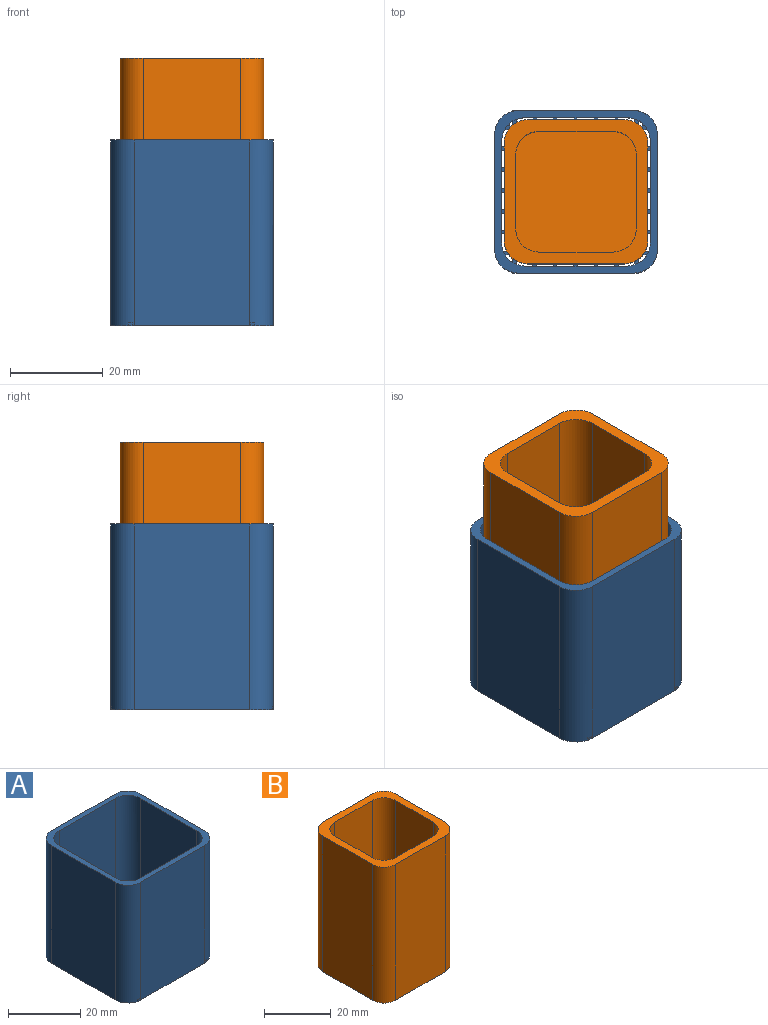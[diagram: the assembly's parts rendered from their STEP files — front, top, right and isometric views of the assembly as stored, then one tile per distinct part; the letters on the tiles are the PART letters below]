
ASSEMBLY  parts=2 mates=1
PART A: 259 faces, bbox 35x35x40 mm
  f0: plane 3.7x0.6mm, normal (-1,0,0), area 2.2mm2, adj f115,f120,f242,f257
  f1: cylinder r=5mm len=40mm, axis (0,0,-1), area 313mm2, adj f17,f112,f114,f115,f120,f137,f138,f257
  f2: plane 3.7x0.6mm, normal (-1,0,0), area 2.2mm2, adj f115,f120,f240,f255
  f3: plane 3.7x0.6mm, normal (1,0,0), area 2.2mm2, adj f115,f120,f240,f255
  f4: plane 3.7x0.6mm, normal (-1,0,0), area 2.2mm2, adj f115,f120,f238,f253
  f5: plane 3.7x0.6mm, normal (1,0,0), area 2.2mm2, adj f115,f120,f238,f253
  f6: plane 3.7x0.6mm, normal (-1,0,0), area 2.2mm2, adj f115,f120,f236,f251
  f7: plane 3.7x0.6mm, normal (1,0,0), area 2.2mm2, adj f115,f120,f236,f251
  f8: plane 3.7x0.6mm, normal (-1,0,0), area 2.2mm2, adj f115,f120,f234,f249
  f9: plane 3.7x0.6mm, normal (1,0,0), area 2.2mm2, adj f115,f120,f234,f249
  f10: plane 3.7x0.6mm, normal (-1,0,0), area 2.2mm2, adj f115,f120,f232,f247
  f11: plane 3.7x0.6mm, normal (1,0,0), area 2.2mm2, adj f115,f120,f232,f247
  f12: plane 3.7x0.6mm, normal (-1,0,0), area 2.2mm2, adj f115,f120,f230,f245
  f13: plane 3.7x0.6mm, normal (1,0,0), area 2.2mm2, adj f115,f120,f230,f245
  f14: plane 3.7x0.6mm, normal (1,0,0), area 2.2mm2, adj f115,f120,f228,f243
  f15: cylinder r=5mm len=40mm, axis (0,0,-1), area 313mm2, adj f31,f112,f114,f115,f120,f121,f122,f243
  f16: plane 3.7x0.6mm, normal (-1,0,0), area 2.2mm2, adj f115,f120,f226,f241
  f17: plane 40x22mm, normal (1,0,0), area 877.6mm2, adj f1,f89,f114,f115,f120,f163,f164,f187
  f18: plane 3.7x0.6mm, normal (-1,0,0), area 2.2mm2, adj f115,f120,f224,f239
  f19: plane 3.7x0.6mm, normal (1,0,0), area 2.2mm2, adj f115,f120,f224,f239
  f20: plane 3.7x0.6mm, normal (-1,0,0), area 2.2mm2, adj f115,f120,f222,f237
  f21: plane 3.7x0.6mm, normal (1,0,0), area 2.2mm2, adj f115,f120,f222,f237
  f22: plane 3.7x0.6mm, normal (-1,0,0), area 2.2mm2, adj f115,f120,f219,f235
  f23: plane 3.7x0.6mm, normal (1,0,0), area 2.2mm2, adj f115,f120,f219,f235
  f24: plane 3.7x0.6mm, normal (-1,0,0), area 2.2mm2, adj f115,f120,f217,f233
  f25: plane 3.7x0.6mm, normal (1,0,0), area 2.2mm2, adj f115,f120,f217,f233
  f26: plane 3.7x0.6mm, normal (-1,0,0), area 2.2mm2, adj f115,f120,f216,f231
  f27: plane 3.7x0.6mm, normal (1,0,0), area 2.2mm2, adj f115,f120,f216,f231
  f28: plane 3.7x0.6mm, normal (-1,0,0), area 2.2mm2, adj f115,f120,f214,f229
  f29: plane 3.7x0.6mm, normal (1,0,0), area 2.2mm2, adj f115,f120,f214,f229
  f30: plane 3.7x0.6mm, normal (1,0,0), area 2.2mm2, adj f115,f120,f212,f227
  f31: plane 40x22mm, normal (-1,0,0), area 877.6mm2, adj f15,f88,f114,f115,f120,f177,f178,f179
  f32: plane 3.7x0.6mm, normal (-1,0,0), area 2.2mm2, adj f115,f120,f210,f225
  f33: plane 3.7x0.6mm, normal (-1,0,0), area 2.2mm2, adj f115,f120,f207,f223
  f34: plane 3.7x0.6mm, normal (1,0,0), area 2.2mm2, adj f115,f120,f207,f223
  f35: plane 3.7x0.6mm, normal (-1,0,0), area 2.2mm2, adj f115,f120,f206,f221
  f36: plane 3.7x0.6mm, normal (1,0,0), area 2.2mm2, adj f115,f120,f206,f221
  f37: plane 3.7x0.6mm, normal (-1,0,0), area 2.2mm2, adj f115,f120,f203,f220
  f38: plane 3.7x0.6mm, normal (1,0,0), area 2.2mm2, adj f115,f120,f203,f220
  f39: plane 3.7x0.6mm, normal (-1,0,0), area 2.2mm2, adj f115,f120,f202,f218
  f40: plane 3.7x0.6mm, normal (1,0,0), area 2.2mm2, adj f115,f120,f202,f218
  f41: plane 3.7x0.6mm, normal (-1,0,0), area 2.2mm2, adj f115,f120,f200,f215
  f42: plane 3.7x0.6mm, normal (1,0,0), area 2.2mm2, adj f115,f120,f200,f215
  f43: plane 3.7x0.6mm, normal (-1,0,0), area 2.2mm2, adj f115,f120,f198,f213
  f44: plane 3.7x0.6mm, normal (1,0,0), area 2.2mm2, adj f115,f120,f198,f213
  f45: plane 3.7x0.6mm, normal (1,0,0), area 2.2mm2, adj f115,f120,f196,f211
  f46: plane 3.7x0.6mm, normal (-1,0,0), area 2.2mm2, adj f115,f120,f188,f209
  f47: plane 3.7x0.6mm, normal (-1,0,0), area 2.2mm2, adj f115,f120,f190,f208
  f48: plane 3.7x0.6mm, normal (1,0,0), area 2.2mm2, adj f115,f120,f190,f208
  f49: plane 3.7x0.6mm, normal (-1,0,0), area 2.2mm2, adj f115,f120,f192,f205
  f50: plane 3.7x0.6mm, normal (1,0,0), area 2.2mm2, adj f115,f120,f192,f205
  f51: plane 3.7x0.6mm, normal (-1,0,0), area 2.2mm2, adj f115,f120,f193,f204
  f52: plane 3.7x0.6mm, normal (1,0,0), area 2.2mm2, adj f115,f120,f193,f204
  f53: plane 3.7x0.6mm, normal (-1,0,0), area 2.2mm2, adj f115,f120,f186,f201
  f54: plane 3.7x0.6mm, normal (1,0,0), area 2.2mm2, adj f115,f120,f186,f201
  f55: plane 3.7x0.6mm, normal (-1,0,0), area 2.2mm2, adj f115,f120,f184,f199
  f56: plane 3.7x0.6mm, normal (1,0,0), area 2.2mm2, adj f115,f120,f184,f199
  f57: plane 3.7x0.6mm, normal (-1,0,0), area 2.2mm2, adj f115,f120,f182,f197
  f58: plane 3.7x0.6mm, normal (1,0,0), area 2.2mm2, adj f115,f120,f182,f197
  f59: plane 3.7x0.6mm, normal (1,0,0), area 2.2mm2, adj f115,f120,f180,f195
  f60: plane 3.7x0.6mm, normal (-1,0,0), area 2.2mm2, adj f115,f120,f169,f194
  f61: plane 3.7x0.6mm, normal (-1,0,0), area 2.2mm2, adj f115,f120,f167,f191
  f62: plane 3.7x0.6mm, normal (1,0,0), area 2.2mm2, adj f115,f120,f169,f194
  f63: plane 3.7x0.6mm, normal (-1,0,0), area 2.2mm2, adj f115,f120,f165,f189
  f64: plane 3.7x0.6mm, normal (1,0,0), area 2.2mm2, adj f115,f120,f167,f191
  f65: plane 3.7x0.6mm, normal (1,0,0), area 2.2mm2, adj f115,f120,f165,f189
  f66: plane 3.7x0.6mm, normal (-1,0,0), area 2.2mm2, adj f115,f120,f163,f187
  f67: plane 3.7x0.6mm, normal (-1,0,0), area 2.2mm2, adj f115,f120,f171,f185
  f68: plane 3.7x0.6mm, normal (1,0,0), area 2.2mm2, adj f115,f120,f171,f185
  f69: plane 3.7x0.6mm, normal (-1,0,0), area 2.2mm2, adj f115,f120,f173,f183
  f70: plane 3.7x0.6mm, normal (1,0,0), area 2.2mm2, adj f115,f120,f173,f183
  f71: plane 3.7x0.6mm, normal (-1,0,0), area 2.2mm2, adj f115,f120,f175,f181
  f72: plane 3.7x0.6mm, normal (1,0,0), area 2.2mm2, adj f115,f120,f175,f181
  f73: plane 3.7x0.6mm, normal (1,0,0), area 2.2mm2, adj f115,f120,f178,f179
  f74: plane 3.7x0.6mm, normal (1,0,0), area 2.2mm2, adj f115,f120,f162,f177
  f75: plane 3.7x0.6mm, normal (-1,0,0), area 2.2mm2, adj f115,f120,f159,f176
  f76: plane 3.7x0.6mm, normal (-1,0,0), area 2.2mm2, adj f115,f120,f157,f174
  f77: plane 3.7x0.6mm, normal (1,0,0), area 2.2mm2, adj f115,f120,f159,f176
  f78: plane 3.7x0.6mm, normal (-1,0,0), area 2.2mm2, adj f115,f120,f155,f172
  f79: plane 3.7x0.6mm, normal (1,0,0), area 2.2mm2, adj f115,f120,f157,f174
  f80: plane 3.7x0.6mm, normal (-1,0,0), area 2.2mm2, adj f115,f120,f153,f170
  f81: plane 3.7x0.6mm, normal (1,0,0), area 2.2mm2, adj f115,f120,f155,f172
  f82: plane 3.7x0.6mm, normal (-1,0,0), area 2.2mm2, adj f115,f120,f151,f168
  f83: plane 3.7x0.6mm, normal (1,0,0), area 2.2mm2, adj f115,f120,f153,f170
  f84: plane 3.7x0.6mm, normal (-1,0,0), area 2.2mm2, adj f115,f120,f149,f166
  f85: plane 3.7x0.6mm, normal (1,0,0), area 2.2mm2, adj f115,f120,f151,f168
  f86: plane 3.7x0.6mm, normal (1,0,0), area 2.2mm2, adj f115,f120,f149,f166
  f87: plane 3.7x0.6mm, normal (-1,0,0), area 2.2mm2, adj f115,f120,f147,f164
  f88: cylinder r=5mm len=40mm, axis (0,0,-1), area 313.1mm2, adj f31,f90,f91,f111,f114,f115,f120,f161
  f89: cylinder r=5mm len=40mm, axis (0,0,-1), area 313.1mm2, adj f17,f102,f103,f111,f114,f115,f120,f147
  f90: plane 1.83x0.6mm, normal (1,0,0), area 1.1mm2, adj f88,f115,f120,f161
  f91: plane 2.2x0.6mm, normal (-1,0,0), area 1.3mm2, adj f88,f115,f120,f160
  f92: plane 2.5x0.6mm, normal (-1,0,0), area 1.5mm2, adj f111,f115,f120,f158
  f93: plane 2.5x0.6mm, normal (1,0,0), area 1.5mm2, adj f111,f115,f120,f160
  f94: plane 2.5x0.6mm, normal (-1,0,0), area 1.5mm2, adj f111,f115,f120,f156
  f95: plane 2.5x0.6mm, normal (1,0,0), area 1.5mm2, adj f111,f115,f120,f158
  f96: plane 2.5x0.6mm, normal (-1,0,0), area 1.5mm2, adj f111,f115,f120,f154
  f97: plane 2.5x0.6mm, normal (1,0,0), area 1.5mm2, adj f111,f115,f120,f156
  f98: plane 2.5x0.6mm, normal (-1,0,0), area 1.5mm2, adj f111,f115,f120,f152
  f99: plane 2.5x0.6mm, normal (1,0,0), area 1.5mm2, adj f111,f115,f120,f154
  f100: plane 2.5x0.6mm, normal (-1,0,0), area 1.5mm2, adj f111,f115,f120,f150
  f101: plane 2.5x0.6mm, normal (1,0,0), area 1.5mm2, adj f111,f115,f120,f152
  f102: plane 2.13x0.6mm, normal (1,0,0), area 1.3mm2, adj f89,f115,f120,f150
  f103: plane 1.71x0.6mm, normal (-1,0,0), area 1mm2, adj f89,f115,f120,f148
  f104: plane 40x25mm, normal (1,0,0), area 1000mm2, adj f105,f113,f114,f115
  f105: cylinder r=5mm len=40mm, axis (0,0,-1), area 313.7mm2, adj f104,f106,f114,f115,f123,f124,f125
  f106: plane 40x25mm, normal (0,1,0), area 1000mm2, adj f105,f107,f114,f115
  f107: cylinder r=5mm len=40mm, axis (0,0,-1), area 313.7mm2, adj f106,f108,f114,f115,f143,f144,f146
  f108: plane 40x25mm, normal (-1,0,0), area 1000mm2, adj f107,f109,f114,f115
  f109: cylinder r=5mm len=40mm, axis (0,0,-1), area 313.7mm2, adj f108,f110,f114,f115,f140,f141,f142
  f110: plane 40x25mm, normal (0,-1,0), area 1000mm2, adj f109,f113,f114,f115
  f111: plane 40x22mm, normal (0,1,0), area 877.6mm2, adj f88,f89,f92,f93,f94,f95,f96,f97
  f112: plane 40x22mm, normal (0,-1,0), area 877.6mm2, adj f1,f15,f114,f115,f120,f127,f128,f129
  f113: cylinder r=5mm len=40mm, axis (0,0,-1), area 313.7mm2, adj f104,f110,f114,f115,f117,f118,f119
  f114: plane 35x35mm, normal (0,0,1), area 201mm2, adj f1,f15,f17,f31,f88,f89,f104,f105
  f115: plane 35x35mm, normal (0,0,-1), area 524.3mm2, adj f0,f1,f2,f3,f4,f5,f6,f7
  f116: plane 0.8x0.6mm, normal (0,-1,0), area 0.5mm2, adj f115,f117,f118,f119
  f117: plane 0.8x0.1mm, normal (0,0,1), area 0mm2, adj f113,f116,f118,f119
  f118: plane 0.6x0.1mm, normal (1,0,0), area 0.1mm2, adj f113,f115,f116,f117
  f119: plane 0.6x0mm, normal (-1,0,0), area 0mm2, adj f113,f115,f116,f117
  f120: plane 32x32mm, normal (0,0,1), area 323.1mm2, adj f0,f1,f2,f3,f4,f5,f6,f7
  f121: plane 1.03x0.6mm, normal (1,0,0), area 0.6mm2, adj f15,f115,f120,f244
  f122: plane 1.4x0.6mm, normal (-1,0,0), area 0.8mm2, adj f15,f115,f120,f246
  f123: plane 0.8x0.1mm, normal (0,0,1), area 0mm2, adj f105,f124,f125,f126
  f124: plane 0.6x0mm, normal (-1,0,0), area 0mm2, adj f105,f115,f123,f126
  f125: plane 0.6x0.1mm, normal (1,0,0), area 0.1mm2, adj f105,f115,f123,f126
  f126: plane 0.8x0.6mm, normal (0,1,0), area 0.5mm2, adj f115,f123,f124,f125
  f127: plane 1.7x0.6mm, normal (-1,0,0), area 1mm2, adj f112,f115,f120,f248
  f128: plane 1.7x0.6mm, normal (1,0,0), area 1mm2, adj f112,f115,f120,f246
  f129: plane 1.7x0.6mm, normal (-1,0,0), area 1mm2, adj f112,f115,f120,f250
  f130: plane 1.7x0.6mm, normal (1,0,0), area 1mm2, adj f112,f115,f120,f248
  f131: plane 1.7x0.6mm, normal (-1,0,0), area 1mm2, adj f112,f115,f120,f252
  f132: plane 1.7x0.6mm, normal (1,0,0), area 1mm2, adj f112,f115,f120,f250
  f133: plane 1.7x0.6mm, normal (-1,0,0), area 1mm2, adj f112,f115,f120,f254
  f134: plane 1.7x0.6mm, normal (1,0,0), area 1mm2, adj f112,f115,f120,f252
  f135: plane 1.7x0.6mm, normal (-1,0,0), area 1mm2, adj f112,f115,f120,f256
  f136: plane 1.7x0.6mm, normal (1,0,0), area 1mm2, adj f112,f115,f120,f254
  f137: plane 1.33x0.6mm, normal (1,0,0), area 0.8mm2, adj f1,f115,f120,f256
  f138: plane 0.91x0.6mm, normal (-1,0,0), area 0.5mm2, adj f1,f115,f120,f258
  f139: plane 0.8x0.6mm, normal (0,-1,0), area 0.5mm2, adj f115,f140,f141,f142
  f140: plane 0.8x0.15mm, normal (0,0,1), area 0.1mm2, adj f109,f139,f141,f142
  f141: plane 0.6x0.02mm, normal (1,0,0), area 0mm2, adj f109,f115,f139,f140
  f142: plane 0.6x0.15mm, normal (-1,0,0), area 0.1mm2, adj f109,f115,f139,f140
  f143: plane 0.6x0.15mm, normal (-1,0,0), area 0.1mm2, adj f107,f115,f145,f146
  f144: plane 0.6x0.02mm, normal (1,0,0), area 0mm2, adj f107,f115,f145,f146
  f145: plane 0.8x0.6mm, normal (0,1,0), area 0.5mm2, adj f115,f143,f144,f146
  f146: plane 0.8x0.15mm, normal (0,0,1), area 0.1mm2, adj f107,f143,f144,f145
  f147: plane 2x0.6mm, normal (0,1,0), area 1.2mm2, adj f87,f89,f115,f120
  f148: plane 1.63x0.6mm, normal (0,-1,0), area 1mm2, adj f89,f103,f115,f120
  f149: plane 3.6x0.6mm, normal (0,1,0), area 2.2mm2, adj f84,f86,f115,f120
  f150: plane 3.6x0.6mm, normal (0,-1,0), area 2.2mm2, adj f100,f102,f115,f120
  f151: plane 3.6x0.6mm, normal (0,1,0), area 2.2mm2, adj f82,f85,f115,f120
  f152: plane 3.6x0.6mm, normal (0,-1,0), area 2.2mm2, adj f98,f101,f115,f120
  f153: plane 3.6x0.6mm, normal (0,1,0), area 2.2mm2, adj f80,f83,f115,f120
  f154: plane 3.6x0.6mm, normal (0,-1,0), area 2.2mm2, adj f96,f99,f115,f120
  f155: plane 3.6x0.6mm, normal (0,1,0), area 2.2mm2, adj f78,f81,f115,f120
  f156: plane 3.6x0.6mm, normal (0,-1,0), area 2.2mm2, adj f94,f97,f115,f120
  f157: plane 3.6x0.6mm, normal (0,1,0), area 2.2mm2, adj f76,f79,f115,f120
  f158: plane 3.6x0.6mm, normal (0,-1,0), area 2.2mm2, adj f92,f95,f115,f120
  f159: plane 3.6x0.6mm, normal (0,1,0), area 2.2mm2, adj f75,f77,f115,f120
  f160: plane 3.6x0.6mm, normal (0,-1,0), area 2.2mm2, adj f91,f93,f115,f120
  f161: plane 1.83x0.6mm, normal (0,-1,0), area 1.1mm2, adj f88,f90,f115,f120
  f162: plane 2.2x0.6mm, normal (0,1,0), area 1.3mm2, adj f74,f88,f115,f120
  f163: plane 2.3x0.6mm, normal (0,1,0), area 1.4mm2, adj f17,f66,f115,f120
  f164: plane 2.3x0.6mm, normal (0,-1,0), area 1.4mm2, adj f17,f87,f115,f120
  f165: plane 3.6x0.6mm, normal (0,1,0), area 2.2mm2, adj f63,f65,f115,f120
  f166: plane 3.6x0.6mm, normal (0,-1,0), area 2.2mm2, adj f84,f86,f115,f120
  f167: plane 3.6x0.6mm, normal (0,1,0), area 2.2mm2, adj f61,f64,f115,f120
  f168: plane 3.6x0.6mm, normal (0,-1,0), area 2.2mm2, adj f82,f85,f115,f120
  f169: plane 3.6x0.6mm, normal (0,1,0), area 2.2mm2, adj f60,f62,f115,f120
  f170: plane 3.6x0.6mm, normal (0,-1,0), area 2.2mm2, adj f80,f83,f115,f120
  f171: plane 3.6x0.6mm, normal (0,1,0), area 2.2mm2, adj f67,f68,f115,f120
  f172: plane 3.6x0.6mm, normal (0,-1,0), area 2.2mm2, adj f78,f81,f115,f120
  f173: plane 3.6x0.6mm, normal (0,1,0), area 2.2mm2, adj f69,f70,f115,f120
  f174: plane 3.6x0.6mm, normal (0,-1,0), area 2.2mm2, adj f76,f79,f115,f120
  f175: plane 3.6x0.6mm, normal (0,1,0), area 2.2mm2, adj f71,f72,f115,f120
  f176: plane 3.6x0.6mm, normal (0,-1,0), area 2.2mm2, adj f75,f77,f115,f120
  f177: plane 2.5x0.6mm, normal (0,-1,0), area 1.5mm2, adj f31,f74,f115,f120
  f178: plane 2.5x0.6mm, normal (0,1,0), area 1.5mm2, adj f31,f73,f115,f120
  f179: plane 2.5x0.6mm, normal (0,-1,0), area 1.5mm2, adj f31,f73,f115,f120
  f180: plane 2.5x0.6mm, normal (0,1,0), area 1.5mm2, adj f31,f59,f115,f120
  f181: plane 3.6x0.6mm, normal (0,-1,0), area 2.2mm2, adj f71,f72,f115,f120
  f182: plane 3.6x0.6mm, normal (0,1,0), area 2.2mm2, adj f57,f58,f115,f120
  f183: plane 3.6x0.6mm, normal (0,-1,0), area 2.2mm2, adj f69,f70,f115,f120
  f184: plane 3.6x0.6mm, normal (0,1,0), area 2.2mm2, adj f55,f56,f115,f120
  f185: plane 3.6x0.6mm, normal (0,-1,0), area 2.2mm2, adj f67,f68,f115,f120
  f186: plane 3.6x0.6mm, normal (0,1,0), area 2.2mm2, adj f53,f54,f115,f120
  f187: plane 2.3x0.6mm, normal (0,-1,0), area 1.4mm2, adj f17,f66,f115,f120
  f188: plane 2.3x0.6mm, normal (0,1,0), area 1.4mm2, adj f17,f46,f115,f120
  f189: plane 3.6x0.6mm, normal (0,-1,0), area 2.2mm2, adj f63,f65,f115,f120
  f190: plane 3.6x0.6mm, normal (0,1,0), area 2.2mm2, adj f47,f48,f115,f120
  f191: plane 3.6x0.6mm, normal (0,-1,0), area 2.2mm2, adj f61,f64,f115,f120
  f192: plane 3.6x0.6mm, normal (0,1,0), area 2.2mm2, adj f49,f50,f115,f120
  f193: plane 3.6x0.6mm, normal (0,1,0), area 2.2mm2, adj f51,f52,f115,f120
  f194: plane 3.6x0.6mm, normal (0,-1,0), area 2.2mm2, adj f60,f62,f115,f120
  f195: plane 2.5x0.6mm, normal (0,-1,0), area 1.5mm2, adj f31,f59,f115,f120
  f196: plane 2.5x0.6mm, normal (0,1,0), area 1.5mm2, adj f31,f45,f115,f120
  f197: plane 3.6x0.6mm, normal (0,-1,0), area 2.2mm2, adj f57,f58,f115,f120
  f198: plane 3.6x0.6mm, normal (0,1,0), area 2.2mm2, adj f43,f44,f115,f120
  f199: plane 3.6x0.6mm, normal (0,-1,0), area 2.2mm2, adj f55,f56,f115,f120
  f200: plane 3.6x0.6mm, normal (0,1,0), area 2.2mm2, adj f41,f42,f115,f120
  f201: plane 3.6x0.6mm, normal (0,-1,0), area 2.2mm2, adj f53,f54,f115,f120
  f202: plane 3.6x0.6mm, normal (0,1,0), area 2.2mm2, adj f39,f40,f115,f120
  f203: plane 3.6x0.6mm, normal (0,1,0), area 2.2mm2, adj f37,f38,f115,f120
  f204: plane 3.6x0.6mm, normal (0,-1,0), area 2.2mm2, adj f51,f52,f115,f120
  f205: plane 3.6x0.6mm, normal (0,-1,0), area 2.2mm2, adj f49,f50,f115,f120
  f206: plane 3.6x0.6mm, normal (0,1,0), area 2.2mm2, adj f35,f36,f115,f120
  f207: plane 3.6x0.6mm, normal (0,1,0), area 2.2mm2, adj f33,f34,f115,f120
  f208: plane 3.6x0.6mm, normal (0,-1,0), area 2.2mm2, adj f47,f48,f115,f120
  f209: plane 2.3x0.6mm, normal (0,-1,0), area 1.4mm2, adj f17,f46,f115,f120
  f210: plane 2.3x0.6mm, normal (0,1,0), area 1.4mm2, adj f17,f32,f115,f120
  f211: plane 2.5x0.6mm, normal (0,-1,0), area 1.5mm2, adj f31,f45,f115,f120
  f212: plane 2.5x0.6mm, normal (0,1,0), area 1.5mm2, adj f30,f31,f115,f120
  f213: plane 3.6x0.6mm, normal (0,-1,0), area 2.2mm2, adj f43,f44,f115,f120
  f214: plane 3.6x0.6mm, normal (0,1,0), area 2.2mm2, adj f28,f29,f115,f120
  f215: plane 3.6x0.6mm, normal (0,-1,0), area 2.2mm2, adj f41,f42,f115,f120
  f216: plane 3.6x0.6mm, normal (0,1,0), area 2.2mm2, adj f26,f27,f115,f120
  f217: plane 3.6x0.6mm, normal (0,1,0), area 2.2mm2, adj f24,f25,f115,f120
  f218: plane 3.6x0.6mm, normal (0,-1,0), area 2.2mm2, adj f39,f40,f115,f120
  f219: plane 3.6x0.6mm, normal (0,1,0), area 2.2mm2, adj f22,f23,f115,f120
  f220: plane 3.6x0.6mm, normal (0,-1,0), area 2.2mm2, adj f37,f38,f115,f120
  f221: plane 3.6x0.6mm, normal (0,-1,0), area 2.2mm2, adj f35,f36,f115,f120
  f222: plane 3.6x0.6mm, normal (0,1,0), area 2.2mm2, adj f20,f21,f115,f120
  f223: plane 3.6x0.6mm, normal (0,-1,0), area 2.2mm2, adj f33,f34,f115,f120
  f224: plane 3.6x0.6mm, normal (0,1,0), area 2.2mm2, adj f18,f19,f115,f120
  f225: plane 2.3x0.6mm, normal (0,-1,0), area 1.4mm2, adj f17,f32,f115,f120
  f226: plane 2.3x0.6mm, normal (0,1,0), area 1.4mm2, adj f16,f17,f115,f120
  f227: plane 2.5x0.6mm, normal (0,-1,0), area 1.5mm2, adj f30,f31,f115,f120
  f228: plane 2.5x0.6mm, normal (0,1,0), area 1.5mm2, adj f14,f31,f115,f120
  f229: plane 3.6x0.6mm, normal (0,-1,0), area 2.2mm2, adj f28,f29,f115,f120
  f230: plane 3.6x0.6mm, normal (0,1,0), area 2.2mm2, adj f12,f13,f115,f120
  f231: plane 3.6x0.6mm, normal (0,-1,0), area 2.2mm2, adj f26,f27,f115,f120
  f232: plane 3.6x0.6mm, normal (0,1,0), area 2.2mm2, adj f10,f11,f115,f120
  f233: plane 3.6x0.6mm, normal (0,-1,0), area 2.2mm2, adj f24,f25,f115,f120
  f234: plane 3.6x0.6mm, normal (0,1,0), area 2.2mm2, adj f8,f9,f115,f120
  f235: plane 3.6x0.6mm, normal (0,-1,0), area 2.2mm2, adj f22,f23,f115,f120
  f236: plane 3.6x0.6mm, normal (0,1,0), area 2.2mm2, adj f6,f7,f115,f120
  f237: plane 3.6x0.6mm, normal (0,-1,0), area 2.2mm2, adj f20,f21,f115,f120
  f238: plane 3.6x0.6mm, normal (0,1,0), area 2.2mm2, adj f4,f5,f115,f120
  f239: plane 3.6x0.6mm, normal (0,-1,0), area 2.2mm2, adj f18,f19,f115,f120
  f240: plane 3.6x0.6mm, normal (0,1,0), area 2.2mm2, adj f2,f3,f115,f120
  f241: plane 2.3x0.6mm, normal (0,-1,0), area 1.4mm2, adj f16,f17,f115,f120
  f242: plane 2.3x0.6mm, normal (0,1,0), area 1.4mm2, adj f0,f17,f115,f120
  f243: plane 1.83x0.6mm, normal (0,-1,0), area 1.1mm2, adj f14,f15,f115,f120
  f244: plane 1.26x0.6mm, normal (0,1,0), area 0.8mm2, adj f15,f115,f120,f121
  f245: plane 3.6x0.6mm, normal (0,-1,0), area 2.2mm2, adj f12,f13,f115,f120
  f246: plane 3.6x0.6mm, normal (0,1,0), area 2.2mm2, adj f115,f120,f122,f128
  f247: plane 3.6x0.6mm, normal (0,-1,0), area 2.2mm2, adj f10,f11,f115,f120
  f248: plane 3.6x0.6mm, normal (0,1,0), area 2.2mm2, adj f115,f120,f127,f130
  f249: plane 3.6x0.6mm, normal (0,-1,0), area 2.2mm2, adj f8,f9,f115,f120
  f250: plane 3.6x0.6mm, normal (0,1,0), area 2.2mm2, adj f115,f120,f129,f132
  f251: plane 3.6x0.6mm, normal (0,-1,0), area 2.2mm2, adj f6,f7,f115,f120
  f252: plane 3.6x0.6mm, normal (0,1,0), area 2.2mm2, adj f115,f120,f131,f134
  f253: plane 3.6x0.6mm, normal (0,-1,0), area 2.2mm2, adj f4,f5,f115,f120
  f254: plane 3.6x0.6mm, normal (0,1,0), area 2.2mm2, adj f115,f120,f133,f136
  f255: plane 3.6x0.6mm, normal (0,-1,0), area 2.2mm2, adj f2,f3,f115,f120
  f256: plane 3.6x0.6mm, normal (0,1,0), area 2.2mm2, adj f115,f120,f135,f137
  f257: plane 1.63x0.6mm, normal (0,-1,0), area 1mm2, adj f0,f1,f115,f120
  f258: plane 1.06x0.6mm, normal (0,1,0), area 0.6mm2, adj f1,f115,f120,f138
PART B: 19 faces, bbox 31x31x50 mm
  f0: plane 50x21mm, normal (1,0,0), area 1050mm2, adj f1,f15,f16,f17
  f1: cylinder r=5mm len=50mm, axis (0,0,-1), area 392.7mm2, adj f0,f2,f16,f17
  f2: plane 50x21mm, normal (0,1,0), area 1050mm2, adj f1,f3,f16,f17
  f3: cylinder r=5mm len=50mm, axis (0,0,-1), area 392.7mm2, adj f2,f4,f16,f17
  f4: plane 50x21mm, normal (-1,0,0), area 1050mm2, adj f3,f5,f16,f17
  f5: cylinder r=5mm len=50mm, axis (0,0,-1), area 392.7mm2, adj f4,f6,f16,f17
  f6: plane 50x21mm, normal (0,-1,0), area 1050mm2, adj f5,f15,f16,f17
  f7: cylinder r=5mm len=48mm, axis (0,0,-1), area 377mm2, adj f8,f14,f16,f18
  f8: plane 48x16mm, normal (-1,0,0), area 768mm2, adj f7,f9,f16,f18
  f9: cylinder r=5mm len=48mm, axis (0,0,-1), area 377mm2, adj f8,f10,f16,f18
  f10: plane 48x16mm, normal (0,1,0), area 768mm2, adj f9,f11,f16,f18
  f11: cylinder r=5mm len=48mm, axis (0,0,-1), area 377mm2, adj f10,f12,f16,f18
  f12: plane 48x16mm, normal (1,0,0), area 768mm2, adj f11,f13,f16,f18
  f13: cylinder r=5mm len=48mm, axis (0,0,-1), area 377mm2, adj f12,f14,f16,f18
  f14: plane 48x16mm, normal (0,-1,0), area 768mm2, adj f7,f13,f16,f18
  f15: cylinder r=5mm len=50mm, axis (0,0,-1), area 392.7mm2, adj f0,f6,f16,f17
  f16: plane 31x31mm, normal (0,0,1), area 285mm2, adj f0,f1,f2,f3,f4,f5,f6,f7
  f17: plane 31x31mm, normal (0,0,-1), area 939.5mm2, adj f0,f1,f2,f3,f4,f5,f6,f15
  f18: plane 26x26mm, normal (0,0,1), area 654.5mm2, adj f7,f8,f9,f10,f11,f12,f13,f14
PLACE A t=(-13.53,-6.07,-24.49)mm fixed
PLACE B t=(-13.53,-6.07,-16.91)mm
MATE slider A.f107 <-> B.f17  axis (0,0,1) through (-26.03,6.43,15.51)mm
